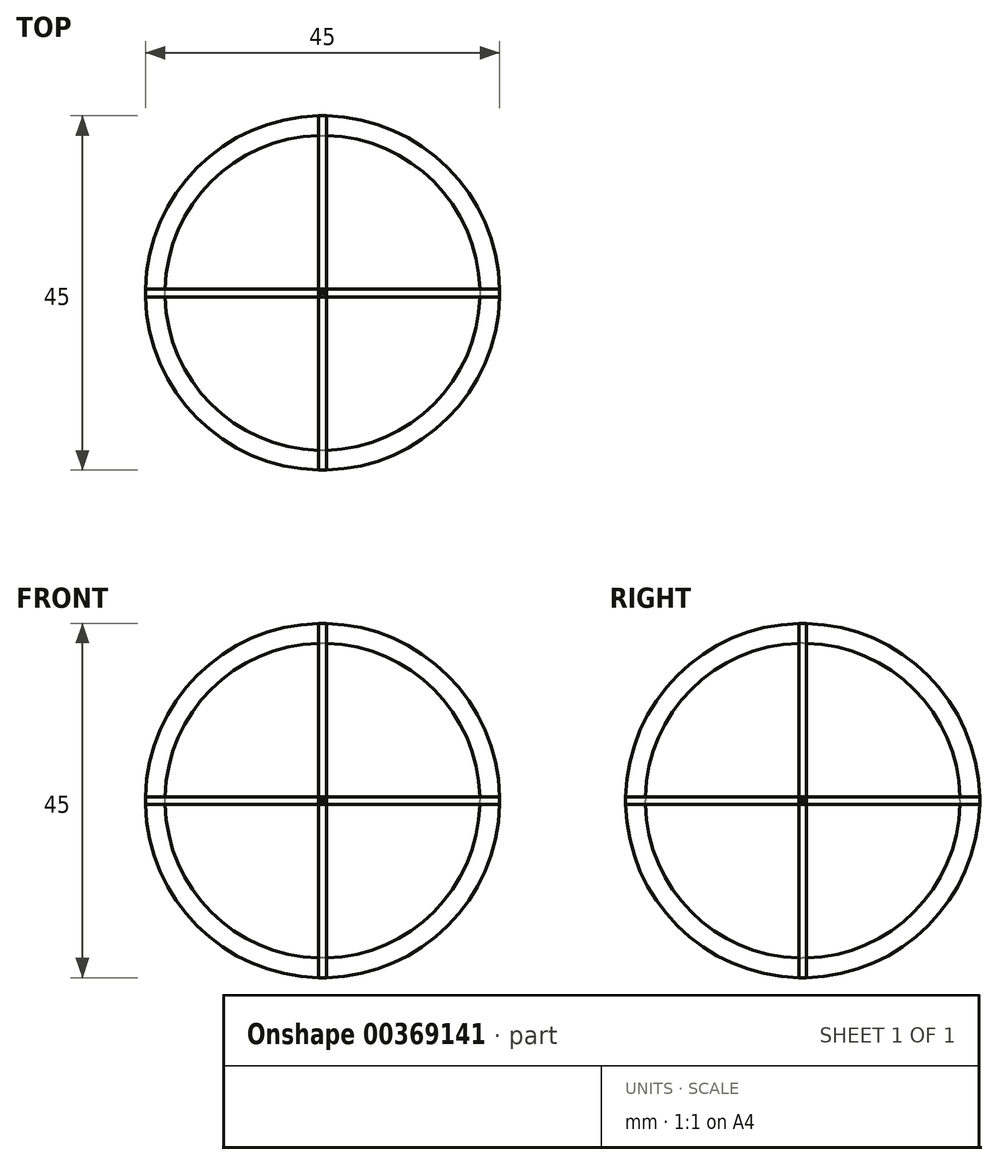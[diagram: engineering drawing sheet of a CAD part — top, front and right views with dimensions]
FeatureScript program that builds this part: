
annotation { "Feature Type Name" : "Feature", "Feature Type Description" : "" }
export const myFeature = defineFeature(function(context is Context, id is Id, definition is map)
    precondition{}
    {
        {
            var Q0;
            Q0=qCreatedBy(makeId("Top.planeOp"),FACE);
            var sketch = newSketch(context, id + "F0", { "sketchPlane" : qUnion([Q0])});
            skCircle(sketch, "E0", {"center": v(0, 0) * mm, "radius": 22.5 * mm});
            skCircle(sketch, "E1", {"center": v(0, 0) * mm, "radius": 20 * mm});
            skSolve(sketch);
        }
        {
            var Q0;
            Q0 = qSketchRegion(id + "F0", true);
            extrude(context, id + "F1", {"entities" : qUnion([Q0]), "depth" : 0.5 * mm, "hasSecondDirection" : true, "secondDirectionOppositeDirection" : true, "secondDirectionDepth" : 0.5 * mm});
        }
        {
            var Q0;
            Q0=qCreatedBy(makeId("Front.planeOp"),FACE);
            var sketch = newSketch(context, id + "F2", { "sketchPlane" : qUnion([Q0])});
            skCircle(sketch, "E2", {"center": v(0, 0) * mm, "radius": 22.5 * mm});
            skCircle(sketch, "E3", {"center": v(0, 0) * mm, "radius": 20 * mm});
            skSolve(sketch);
        }
        {
            var Q0;
            Q0 = qSketchRegion(id + "F2", true);
            extrude(context, id + "F3", {"entities" : qUnion([Q0]), "operationType" : NewBodyOperationType.ADD, "depth" : 0.5 * mm, "hasSecondDirection" : true, "secondDirectionOppositeDirection" : true, "secondDirectionDepth" : 0.5 * mm});
        }
        {
            var Q0;
            Q0=qCreatedBy(makeId("Right.planeOp"),FACE);
            var sketch = newSketch(context, id + "F4", { "sketchPlane" : qUnion([Q0])});
            skCircle(sketch, "E4", {"center": v(0, 0) * mm, "radius": 22.5 * mm});
            skCircle(sketch, "E5", {"center": v(0, 0) * mm, "radius": 20 * mm});
            skSolve(sketch);
        }
        {
            var Q0;
            Q0 = qSketchRegion(id + "F4", true);
            extrude(context, id + "F5", {"entities" : qUnion([Q0]), "operationType" : NewBodyOperationType.ADD, "depth" : 0.5 * mm, "hasSecondDirection" : true, "secondDirectionOppositeDirection" : true, "secondDirectionDepth" : 0.5 * mm});
        }
    });
